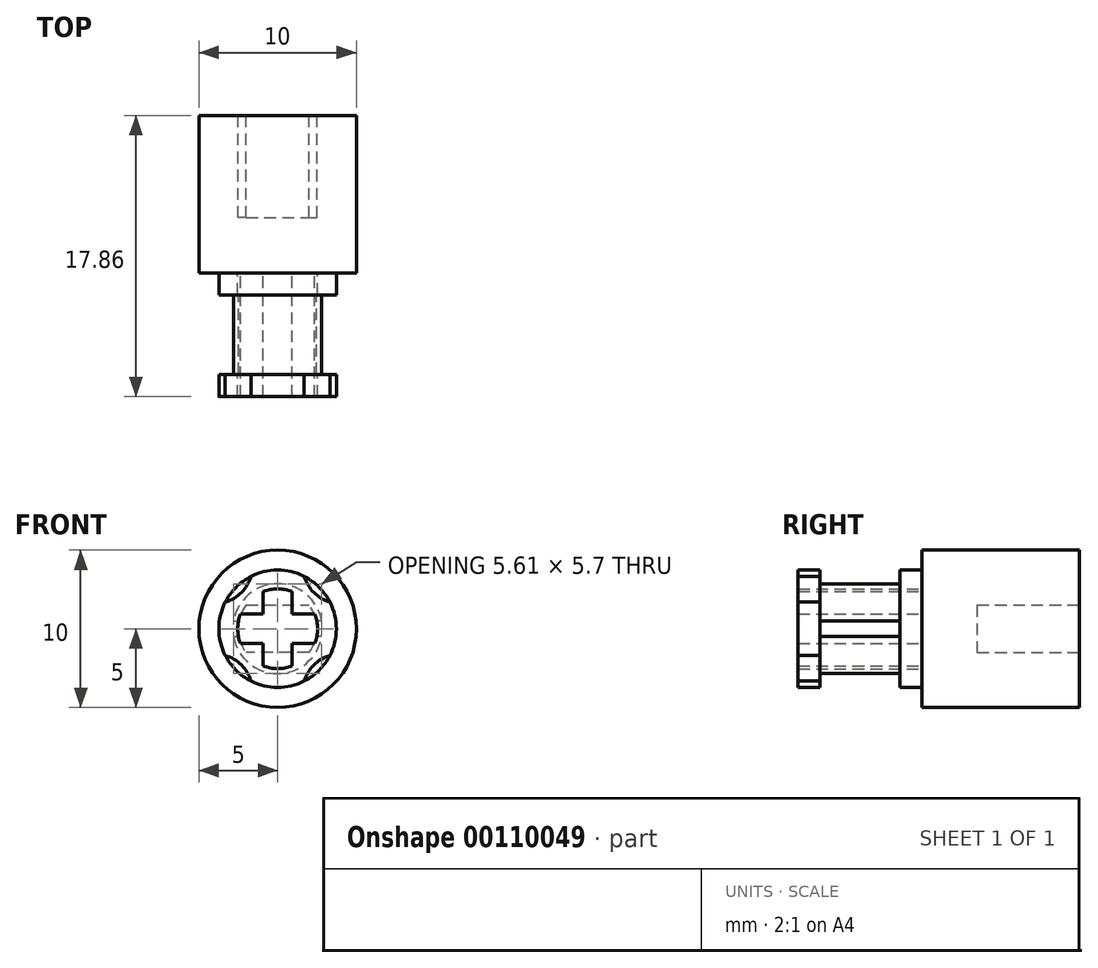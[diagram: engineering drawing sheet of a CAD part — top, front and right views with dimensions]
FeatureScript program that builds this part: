
annotation { "Feature Type Name" : "Feature", "Feature Type Description" : "" }
export const myFeature = defineFeature(function(context is Context, id is Id, definition is map)
    precondition{}
    {
        {
            var Q0;
            Q0=qCreatedBy(makeId("Front.planeOp"),FACE);
            var sketch = newSketch(context, id + "F0", { "sketchPlane" : qUnion([Q0])});
            skCircle(sketch, "E0", {"center": v(0, 0) * mm, "radius": 3.73 * mm});
            skSolve(sketch);
        }
        {
            var Q0;
            Q0=qCreatedBy(makeId("Front.planeOp"),FACE);
            var sketch = newSketch(context, id + "F1", { "sketchPlane" : qUnion([Q0])});
            skLineSegment(sketch, "E1", {"start": v(0.93, 2.36) * mm, "end": v(0.93, 0.93) * mm});
            skLineSegment(sketch, "E2", {"start": v(0.93, 0.93) * mm, "end": v(2.36, 0.93) * mm});
            skLineSegment(sketch, "E3", {"start": v(2.36, -0.93) * mm, "end": v(0.93, -0.93) * mm});
            skLineSegment(sketch, "E4", {"start": v(0.93, -0.93) * mm, "end": v(0.93, -2.36) * mm});
            skLineSegment(sketch, "E5", {"start": v(-0.93, -2.36) * mm, "end": v(-0.93, -0.93) * mm});
            skLineSegment(sketch, "E6", {"start": v(-0.93, -0.93) * mm, "end": v(-2.36, -0.93) * mm});
            skLineSegment(sketch, "E7", {"start": v(-2.36, 0.93) * mm, "end": v(-0.93, 0.93) * mm});
            skLineSegment(sketch, "E8", {"start": v(-0.93, 0.93) * mm, "end": v(-0.93, 2.36) * mm});
            skCircle(sketch, "E9", {"center": v(0, 0) * mm, "radius": 2.54 * mm});
            skCircle(sketch, "E10", {"center": v(0, 0) * mm, "radius": 2.85 * mm});
            skSolve(sketch);
        }
        {
            var Q0;
            Q0=qCreatedBy(makeId("Front.planeOp"),FACE);
            var sketch = newSketch(context, id + "F2", { "sketchPlane" : qUnion([Q0])});
            skCircle(sketch, "E11", {"center": v(0, 0) * mm, "radius": 2.85 * mm});
            skSolve(sketch);
        }
        {
            var Q0;
            Q0=makeQuery(id+"F0.imprint","IMPRINT",FACE,{"disambiguationData":[TD([[makeQuery(id+"F0.imprint","IMPRINT",EDGE,{"derivedFrom":sQuery(id+"F0.wireOp",EDGE,"E0")}),1.0]])]});
            extrude(context, id + "F3", {"entities" : qUnion([Q0]), "depth" : 1.4 * mm});
        }
        {
            var Q0;
            Q0=makeQuery(id+"F2.imprint","IMPRINT",FACE,{"disambiguationData":[TD([[makeQuery(id+"F2.imprint","IMPRINT",EDGE,{"derivedFrom":sQuery(id+"F2.wireOp",EDGE,"E11")}),1.0]])]});
            var Q1;
            Q1=sQuery(id+"F2.wireOp",EDGE,"E11");
            extrude(context, id + "F4", {"entities" : qUnion([Q0]), "operationType" : NewBodyOperationType.REMOVE, "surfaceEntities" : qUnion([Q1]), "depth" : 1.4 * mm});
        }
        {
            var Q0;
            Q0=makeQuery(id+"F1.imprint","IMPRINT",FACE,{"disambiguationData":[TD([[makeQuery(id+"F1.imprint","IMPRINT",EDGE,{"derivedFrom":sQuery(id+"F1.wireOp",EDGE,"E10")}),1.0]])]});
            var Q1;
            Q1=sQuery(id+"F2.wireOp",EDGE,"E11");
            var Q2;
            Q2=sQuery(id+"F1.wireOp",EDGE,"E9");
            extrude(context, id + "F5", {"entities" : qUnion([Q0]), "operationType" : NewBodyOperationType.ADD, "surfaceEntities" : qUnion([Q1, Q2]), "depth" : 7.86 * mm});
        }
        {
            var Q0;
            {var subQ0=sQuery(id+"F1.wireOp",EDGE,"E1");Q0=makeQuery(id+"F1.imprint","IMPRINT",FACE,{"disambiguationData":[TD([[makeQuery(id+"F1.imprint","IMPRINT",EDGE,{"derivedFrom":subQ0}),1.0]])]});}
            extrude(context, id + "F6", {"entities" : qUnion([Q0]), "operationType" : NewBodyOperationType.ADD, "depth" : 7.86 * mm});
        }
        {
            var Q0;
            {var subQ0=sQuery(id+"F1.wireOp",EDGE,"E5");Q0=makeQuery(id+"F1.imprint","IMPRINT",FACE,{"disambiguationData":[TD([[makeQuery(id+"F1.imprint","IMPRINT",EDGE,{"derivedFrom":subQ0}),1.0]])]});}
            extrude(context, id + "F7", {"entities" : qUnion([Q0]), "operationType" : NewBodyOperationType.ADD, "depth" : 7.86 * mm});
        }
        {
            var Q0;
            {var subQ0=sQuery(id+"F1.wireOp",EDGE,"E7");Q0=makeQuery(id+"F1.imprint","IMPRINT",FACE,{"disambiguationData":[TD([[makeQuery(id+"F1.imprint","IMPRINT",EDGE,{"derivedFrom":subQ0}),1.0]])]});}
            extrude(context, id + "F8", {"entities" : qUnion([Q0]), "operationType" : NewBodyOperationType.ADD, "depth" : 7.86 * mm});
        }
        {
            var Q0;
            {var subQ0=sQuery(id+"F1.wireOp",EDGE,"E3");Q0=makeQuery(id+"F1.imprint","IMPRINT",FACE,{"disambiguationData":[TD([[makeQuery(id+"F1.imprint","IMPRINT",EDGE,{"derivedFrom":subQ0}),1.0]])]});}
            extrude(context, id + "F9", {"entities" : qUnion([Q0]), "operationType" : NewBodyOperationType.ADD, "depth" : 7.86 * mm});
        }
        {
            var Q0;
            {var subQ0=sQuery(id+"F1.wireOp",EDGE,"E9");Q0=makeQuery(id+"F9.boolean.opBoolean","MERGE",FACE,{"derivedFrom":[makeQuery(id+"F8.boolean.opBoolean","MERGE",FACE,{"derivedFrom":[makeQuery(id+"F7.boolean.opBoolean","MERGE",FACE,{"derivedFrom":[makeQuery(id+"F6.boolean.opBoolean","MERGE",FACE,{"derivedFrom":[makeQuery(id+"F5.opExtrude","CAP_FACE",FACE,{"disambiguationData":[OSD([subQ0,sQuery(id+"F1.wireOp",EDGE,"E10")])],"isStart":false}),makeQuery(id+"F6.opExtrude","CAP_FACE",FACE,{"disambiguationData":[OSD([sQuery(id+"F1.wireOp",EDGE,"E1"),sQuery(id+"F1.wireOp",EDGE,"E2"),subQ0])],"isStart":false})]}),makeQuery(id+"F7.opExtrude","CAP_FACE",FACE,{"disambiguationData":[OSD([sQuery(id+"F1.wireOp",EDGE,"E5"),sQuery(id+"F1.wireOp",EDGE,"E6"),subQ0])],"isStart":false})]}),makeQuery(id+"F8.opExtrude","CAP_FACE",FACE,{"disambiguationData":[OSD([sQuery(id+"F1.wireOp",EDGE,"E7"),sQuery(id+"F1.wireOp",EDGE,"E8"),subQ0])],"isStart":false})]}),makeQuery(id+"F9.opExtrude","CAP_FACE",FACE,{"disambiguationData":[OSD([sQuery(id+"F1.wireOp",EDGE,"E3"),sQuery(id+"F1.wireOp",EDGE,"E4"),subQ0])],"isStart":false})]});}
            var sketch = newSketch(context, id + "F10", { "sketchPlane" : qUnion([Q0])});
            skPoint(sketch, "E12.endSnap0", {"position": v(2.54, 0) * mm});
            skArc(sketch, "E13", {"start": v(-3.32, 1.7) * mm, "mid": v(-2.3, 2.3) * mm, "end": v(-1.7, 3.32) * mm});
            skArc(sketch, "E14", {"start": v(1.7, 3.32) * mm, "mid": v(2.3, 2.3) * mm, "end": v(3.32, 1.7) * mm});
            skArc(sketch, "E15", {"start": v(3.32, -1.7) * mm, "mid": v(2.3, -2.3) * mm, "end": v(1.7, -3.32) * mm});
            skArc(sketch, "E16", {"start": v(-1.7, -3.32) * mm, "mid": v(-2.3, -2.3) * mm, "end": v(-3.32, -1.7) * mm});
            skArc(sketch, "E17", {"start": v(-3.32, 1.7) * mm, "mid": v(-3.73, 0) * mm, "end": v(-3.32, -1.7) * mm});
            skArc(sketch, "E18.trimOffspring", {"start": v(1.7, 3.32) * mm, "mid": v(0, 3.73) * mm, "end": v(-1.7, 3.32) * mm});
            skArc(sketch, "E19.trimOffspring", {"start": v(3.32, -1.7) * mm, "mid": v(3.73, 0) * mm, "end": v(3.32, 1.7) * mm});
            skArc(sketch, "E20.trimOffspring", {"start": v(-1.7, -3.32) * mm, "mid": v(0, -3.73) * mm, "end": v(1.7, -3.32) * mm});
            skSolve(sketch);
        }
        {
            var Q0;
            Q0=makeQuery(id+"F10.imprint","IMPRINT",FACE,{"disambiguationData":[TD([[makeQuery(id+"F10.imprint","IMPRINT",EDGE,{"derivedFrom":sQuery(id+"F10.wireOp",EDGE,"E13")}),-1.0]])]});
            extrude(context, id + "F11", {"entities" : qUnion([Q0]), "operationType" : NewBodyOperationType.ADD, "oppositeDirection" : true, "depth" : 1.4 * mm});
        }
        {
            var Q0;
            Q0=qCreatedBy(makeId("Right.planeOp"),FACE);
            var sketch = newSketch(context, id + "F12", { "sketchPlane" : qUnion([Q0])});
            skLineSegment(sketch, "E21", {"start": v(-1.4, 0.5) * mm, "end": v(-6.46, 0.5) * mm});
            skLineSegment(sketch, "E22", {"start": v(-6.46, 0.5) * mm, "end": v(-6.46, -0.5) * mm});
            skLineSegment(sketch, "E23", {"start": v(-6.46, -0.5) * mm, "end": v(-1.4, -0.5) * mm});
            skLineSegment(sketch, "E24", {"start": v(-1.4, -0.5) * mm, "end": v(-1.4, 0.5) * mm});
            skSolve(sketch);
        }
        {
            var Q0;
            Q0 = qSketchRegion(id + "F12", true);
            extrude(context, id + "F13", {"entities" : qUnion([Q0]), "operationType" : NewBodyOperationType.REMOVE, "oppositeDirection" : true, "depth" : 8 * mm});
        }
        {
            var Q0;
            Q0=qCreatedBy(makeId("Right.planeOp"),FACE);
            var sketch = newSketch(context, id + "F14", { "sketchPlane" : qUnion([Q0])});
            skLineSegment(sketch, "E25", {"start": v(-1.4, 0.5) * mm, "end": v(-6.46, 0.5) * mm});
            skLineSegment(sketch, "E26", {"start": v(-6.46, 0.5) * mm, "end": v(-6.46, -0.5) * mm});
            skLineSegment(sketch, "E27", {"start": v(-6.46, -0.5) * mm, "end": v(-1.4, -0.5) * mm});
            skLineSegment(sketch, "E28", {"start": v(-1.4, -0.5) * mm, "end": v(-1.4, 0.5) * mm});
            skSolve(sketch);
        }
        {
            var Q0;
            Q0 = qSketchRegion(id + "F14", true);
            extrude(context, id + "F15", {"entities" : qUnion([Q0]), "operationType" : NewBodyOperationType.REMOVE, "depth" : 8 * mm});
        }
        {
            var Q0;
            Q0=qCreatedBy(makeId("Front.planeOp"),FACE);
            cPlane(context, id + "F16", {"entities" : qUnion([Q0]), "cplaneType" : CPlaneType.OFFSET, "offset" : 10 * mm, "oppositeDirection" : true, "width" : 150 * mm, "height" : 150 * mm});
        }
        {
            var Q0;
            Q0=qCreatedBy(id+"F16.planeOp",FACE);
            var sketch = newSketch(context, id + "F17", { "sketchPlane" : qUnion([Q0])});
            skCircle(sketch, "E29", {"center": v(0, 0) * mm, "radius": 5 * mm});
            skSolve(sketch);
        }
        {
            var Q0;
            Q0 = qSketchRegion(id + "F17", true);
            extrude(context, id + "F18", {"entities" : qUnion([Q0]), "operationType" : NewBodyOperationType.ADD, "depth" : 10 * mm});
        }
        {
            var Q0;
            Q0=qCreatedBy(id+"F16.planeOp",FACE);
            var sketch = newSketch(context, id + "F19", { "sketchPlane" : qUnion([Q0])});
            skArc(sketch, "E30", {"start": v(-2, 1.5) * mm, "mid": v(-2.5, 0) * mm, "end": v(-2, -1.5) * mm});
            skLineSegment(sketch, "E31", {"start": v(-2, 1.5) * mm, "end": v(2, 1.5) * mm});
            skLineSegment(sketch, "E32", {"start": v(2, -1.5) * mm, "end": v(-2, -1.5) * mm});
            skArc(sketch, "E33.trimOffspring", {"start": v(2, -1.5) * mm, "mid": v(2.5, 0) * mm, "end": v(2, 1.5) * mm});
            skSolve(sketch);
        }
        {
            var Q0;
            Q0=makeQuery(id+"F19.imprint","IMPRINT",FACE,{"disambiguationData":[TD([[makeQuery(id+"F19.imprint","IMPRINT",EDGE,{"derivedFrom":sQuery(id+"F19.wireOp",EDGE,"E30")}),1.0]])]});
            extrude(context, id + "F20", {"entities" : qUnion([Q0]), "operationType" : NewBodyOperationType.REMOVE, "depth" : 6.5 * mm});
        }
    });
